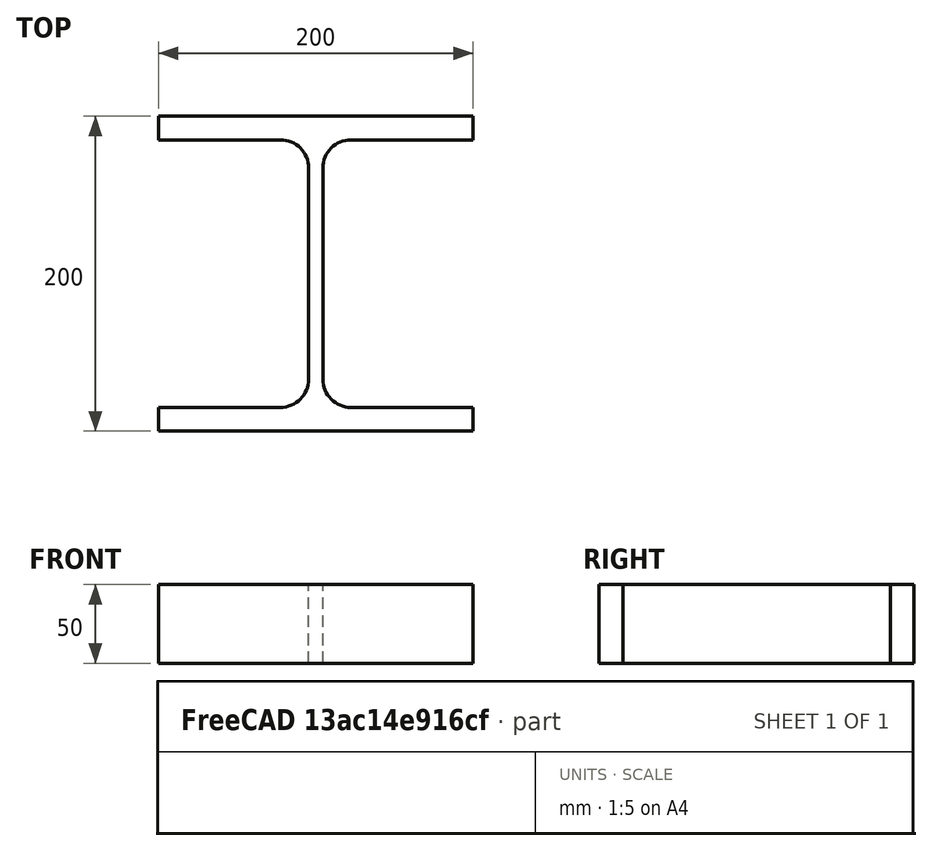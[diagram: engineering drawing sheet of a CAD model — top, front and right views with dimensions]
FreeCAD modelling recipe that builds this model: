
FCSTD DOCUMENT  (FreeCAD 0.15R4671 (Git))
Label: HE-B-Profile 200 DIN1025-2 S235JR
License: All rights reserved
LicenseURL: http://en.wikipedia.org/wiki/All_rights_reserved
objects: Sketcher::SketchObject×1, Part::Extrusion×1
note: 2 computed .brp shape members not serialized (recipe doc carries the construction recipe); baked Part::Feature solids carry a one-line shape summary decoded from their .brp

FEATURE [Sketcher::SketchObject] Sketch
  sketch-geometry (16):
    g0: LineSegment StartX=4.5 StartY=-67 StartZ=0 EndX=4.5 EndY=67 EndZ=0
    g1: LineSegment StartX=22.5 StartY=85 StartZ=0 EndX=100 EndY=85 EndZ=0
    g2: LineSegment StartX=100 StartY=85 StartZ=0 EndX=100 EndY=100 EndZ=0
    g3: LineSegment StartX=100 StartY=100 StartZ=0 EndX=-100 EndY=100 EndZ=0
    g4: LineSegment StartX=-100 StartY=100 StartZ=0 EndX=-100 EndY=85 EndZ=0
    g5: LineSegment StartX=-100 StartY=85 StartZ=0 EndX=-22.5 EndY=85 EndZ=0
    g6: LineSegment StartX=-4.5 StartY=67 StartZ=0 EndX=-4.5 EndY=-67 EndZ=0
    g7: LineSegment StartX=-22.5 StartY=-85 StartZ=0 EndX=-100 EndY=-85 EndZ=0
    g8: LineSegment StartX=-100 StartY=-85 StartZ=0 EndX=-100 EndY=-100 EndZ=0
    g9: LineSegment StartX=-100 StartY=-100 StartZ=0 EndX=100 EndY=-100 EndZ=0
    g10: LineSegment StartX=100 StartY=-100 StartZ=0 EndX=100 EndY=-85 EndZ=0
    g11: LineSegment StartX=100 StartY=-85 StartZ=0 EndX=22.5 EndY=-85 EndZ=0
    g12: ArcOfCircle CenterX=22.5 CenterY=67 CenterZ=0 NormalX=0 NormalY=0 NormalZ=1 Radius=18 StartAngle=1.5708 EndAngle=3.14159
    g13: ArcOfCircle CenterX=22.5 CenterY=-67 CenterZ=0 NormalX=0 NormalY=0 NormalZ=1 Radius=18 StartAngle=3.14159 EndAngle=4.71239
    g14: ArcOfCircle CenterX=-22.5 CenterY=67 CenterZ=0 NormalX=0 NormalY=0 NormalZ=1 Radius=18 StartAngle=0 EndAngle=1.5708
    g15: ArcOfCircle CenterX=-22.5 CenterY=-67 CenterZ=0 NormalX=0 NormalY=0 NormalZ=1 Radius=18 StartAngle=4.71239 EndAngle=6.28319
  constraints (42):
    c: Vertical(g0)
    c: Coincident(g2,g1)
    c: Vertical(g2)
    c: Coincident(g3,g2)
    c: Coincident(g4,g3)
    c: Vertical(g4)
    c: Coincident(g5,g4)
    c: Horizontal(g5)
    c: Vertical(g6)
    c: Horizontal(g7)
    c: Coincident(g8,g7)
    c: Vertical(g8)
    c: Coincident(g9,g8)
    c: Horizontal(g9)
    c: Coincident(g10,g9)
    c: Vertical(g10)
    c: Coincident(g11,g10)
    c: Horizontal(g11)
    c: Tangent(g1,g12) = 1.5708
    c: Tangent(g0,g12) = 1.5708
    c: Tangent(g0,g13) = 1.5708
    c: Tangent(g11,g13) = 1.5708
    c: Tangent(g5,g14) = 1.5708
    c: Tangent(g6,g14) = 1.5708
    c: Tangent(g6,g15) = 1.5708
    c: Tangent(g7,g15) = 1.5708
    c: Equal(g3,g9)
    c: Equal(g2,g4)
    c: Equal(g4,g8)
    c: Equal(g8,g10)
    c: Equal(g12,g14)
    c: Equal(g14,g15)
    c: Equal(g15,g13)
    c: Symmetric(g2,g3,g-2)
    c: Symmetric(g9,g8,g-2)
    c: Symmetric(g0,g6,g-2)
    c: Symmetric(g2,g9,g-1)
    c: DistanceY(g2,g9) = -200
    c: DistanceX(g3) = -200
    c: DistanceX(g0,g6) = -9
    c: DistanceY(g2) = 15
    c: Radius(g12) = 18
FEATURE [Part::Extrusion] Extrude  label="HE-B-Profile 200 DIN1025-2 S235JR"
  Base = -> Sketch
  Dir = (0,0,50)
  Solid = true
